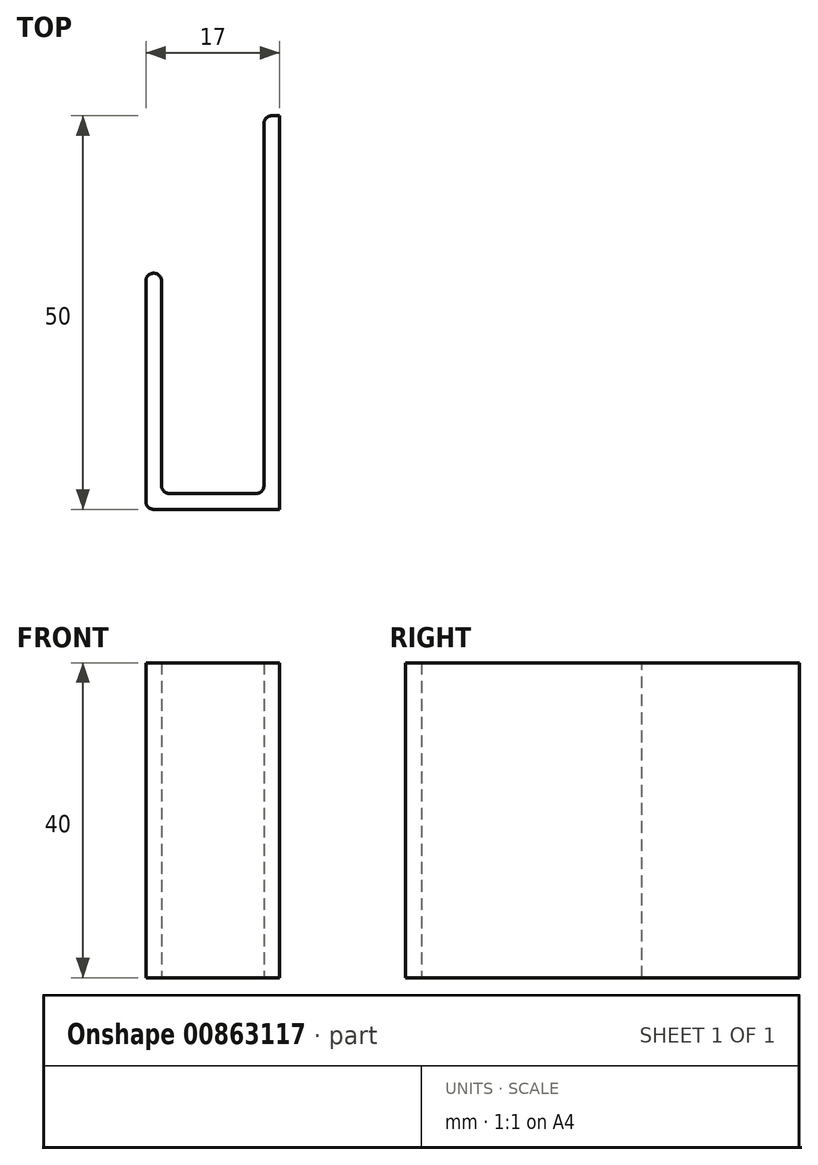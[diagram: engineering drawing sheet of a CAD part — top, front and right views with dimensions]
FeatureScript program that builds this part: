
annotation { "Feature Type Name" : "Feature", "Feature Type Description" : "" }
export const myFeature = defineFeature(function(context is Context, id is Id, definition is map)
    precondition{}
    {
        {
            var Q0;
            Q0=qCreatedBy(makeId("Top.planeOp"),FACE);
            var sketch = newSketch(context, id + "F0", { "sketchPlane" : qUnion([Q0])});
            skLineSegment(sketch, "E0.bottom", {"start": v(-26.58, 17.76) * mm, "end": v(-24.58, 17.76) * mm});
            skLineSegment(sketch, "E0.top", {"start": v(-26.58, -12.24) * mm, "end": v(-24.58, -12.24) * mm});
            skLineSegment(sketch, "E0.left", {"start": v(-26.58, 17.76) * mm, "end": v(-26.58, -12.24) * mm});
            skLineSegment(sketch, "E0.right", {"start": v(-24.58, 17.76) * mm, "end": v(-24.58, -12.24) * mm});
            skLineSegment(sketch, "E1.bottom", {"start": v(-24.58, -12.24) * mm, "end": v(-11.58, -12.24) * mm});
            skLineSegment(sketch, "E1.top", {"start": v(-24.58, -10.24) * mm, "end": v(-11.58, -10.24) * mm});
            skLineSegment(sketch, "E1.left", {"start": v(-24.58, -12.24) * mm, "end": v(-24.58, -10.24) * mm});
            skLineSegment(sketch, "E1.right", {"start": v(-11.58, -12.24) * mm, "end": v(-11.58, -10.24) * mm});
            skLineSegment(sketch, "E2.bottom", {"start": v(-11.58, -12.24) * mm, "end": v(-9.58, -12.24) * mm});
            skLineSegment(sketch, "E2.top", {"start": v(-11.58, 37.76) * mm, "end": v(-9.58, 37.76) * mm});
            skLineSegment(sketch, "E2.left", {"start": v(-11.58, -12.24) * mm, "end": v(-11.58, 37.76) * mm});
            skLineSegment(sketch, "E2.right", {"start": v(-9.58, -12.24) * mm, "end": v(-9.58, 37.76) * mm});
            skSolve(sketch);
        }
        {
            var Q0;
            Q0=qSketchRegion(id+"F0",true);
            extrude(context, id + "F1", {"entities" : qUnion([Q0]), "depth" : 40 * mm, "offsetDistance" : 25 * mm});
        }
        {
            var Q0;
            Q0=makeQuery(id+"F1.opExtrude","SWEPT_EDGE",EDGE,{"disambiguationData":[OSD([sQuery(id+"F0.wireOp",EDGE,"E0.bottom"),sQuery(id+"F0.wireOp",EDGE,"E0.left")])]});
            var Q1;
            Q1=makeQuery(id+"F1.opExtrude","SWEPT_EDGE",EDGE,{"disambiguationData":[OSD([sQuery(id+"F0.wireOp",EDGE,"E0.bottom"),sQuery(id+"F0.wireOp",EDGE,"E0.right")])]});
            var Q2;
            Q2=makeQuery(id+"F1.opExtrude","SWEPT_EDGE",EDGE,{"disambiguationData":[OSD([sQuery(id+"F0.wireOp",EDGE,"E2.top"),sQuery(id+"F0.wireOp",EDGE,"E2.left")])]});
            var Q3;
            Q3=makeQuery(id+"F1.opExtrude","SWEPT_EDGE",EDGE,{"disambiguationData":[OSD([sQuery(id+"F0.wireOp",EDGE,"E0.top"),sQuery(id+"F0.wireOp",EDGE,"E0.left")])]});
            var Q4;
            Q4=makeQuery(id+"F1.opExtrude","SWEPT_EDGE",EDGE,{"disambiguationData":[OSD([sQuery(id+"F0.wireOp",EDGE,"E0.right"),sQuery(id+"F0.wireOp",EDGE,"E1.top"),sQuery(id+"F0.wireOp",EDGE,"E1.left")])]});
            var Q5;
            Q5=makeQuery(id+"F1.opExtrude","SWEPT_EDGE",EDGE,{"disambiguationData":[OSD([sQuery(id+"F0.wireOp",EDGE,"E1.top"),sQuery(id+"F0.wireOp",EDGE,"E2.left")])]});
            fillet(context, id + "F2", {"entities" : qUnion([Q0, Q1, Q2, Q3, Q4, Q5]), "radius" : 1 * mm, "tangentPropagation" : true, "allowEdgeOverflow" : false});
        }
    });
